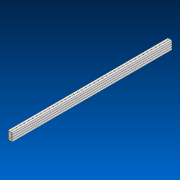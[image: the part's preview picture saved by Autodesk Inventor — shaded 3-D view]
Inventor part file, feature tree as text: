
AUTODESK INVENTOR PART (.ipt)
format: ipt  version: 2022.2 (Build 262287000, 287)  size: 545,280 bytes
history: native  units: in
note: dims shown in document units (in); Inventor stores cm internally (conversion verified against a paired STEP export)
features: other x40, extrude x1, pattern_linear x1, sketch x1
ambient origin geometry x8: Origin, YZ Plane, XZ Plane, XY Plane, X Axis, Y Axis, Z Axis, Center Point
bodies: Solid1 (feature_tree)
feature tree (43):
  extrude  "Extrusion1"  Depth=2.0in
  other  "Work Axis1"
  pattern_linear  "Rectangular Pattern1"  Spacing1=20.0in  [1 undecoded]
  sketch  "Sketch1"  dims[d0=1.0in d1=2.0in d2=20.0in d3=0.0in d4=15.3543in d6=1.0in]
  other  "Work Axis2"
  other  "Work Axis3"
  other  "Work Axis4"
  other  "Work Axis5"
  other  "Work Axis6"
  other  "Work Axis7"
  other  "Work Axis8"
  other  "Work Axis9"
  other  "Work Axis10"
  other  "Work Axis60"
  other  "Work Axis61"
  other  "Work Axis62"
  other  "Work Axis63"
  other  "Work Axis64"
  other  "Work Axis65"
  other  "Work Axis66"
  other  "Work Axis67"
  other  "Work Axis68"
  other  "Work Axis69"
  other  "Work Axis70"
  other  "Work Axis71"
  other  "Work Axis72"
  other  "Work Axis73"
  other  "Work Axis74"
  other  "Work Axis75"
  other  "Work Axis76"
  other  "Work Axis77"
  other  "Work Axis78"
  other  "Work Axis79"
  other  "Work Axis80"
  other  "Work Axis81"
  other  "Work Axis82"
  other  "Work Axis83"
  other  "Work Axis84"
  other  "Work Axis85"
  other  "Work Axis86"
  other  "Work Axis87"
  other  "Work Axis88"
  other  "Cut-Extrude2"
note: 1 required parameter value undecoded (feature->parameter linkage not recoverable at this tier; creation-order binding heuristic only, values carry confidence <= 0.55)
